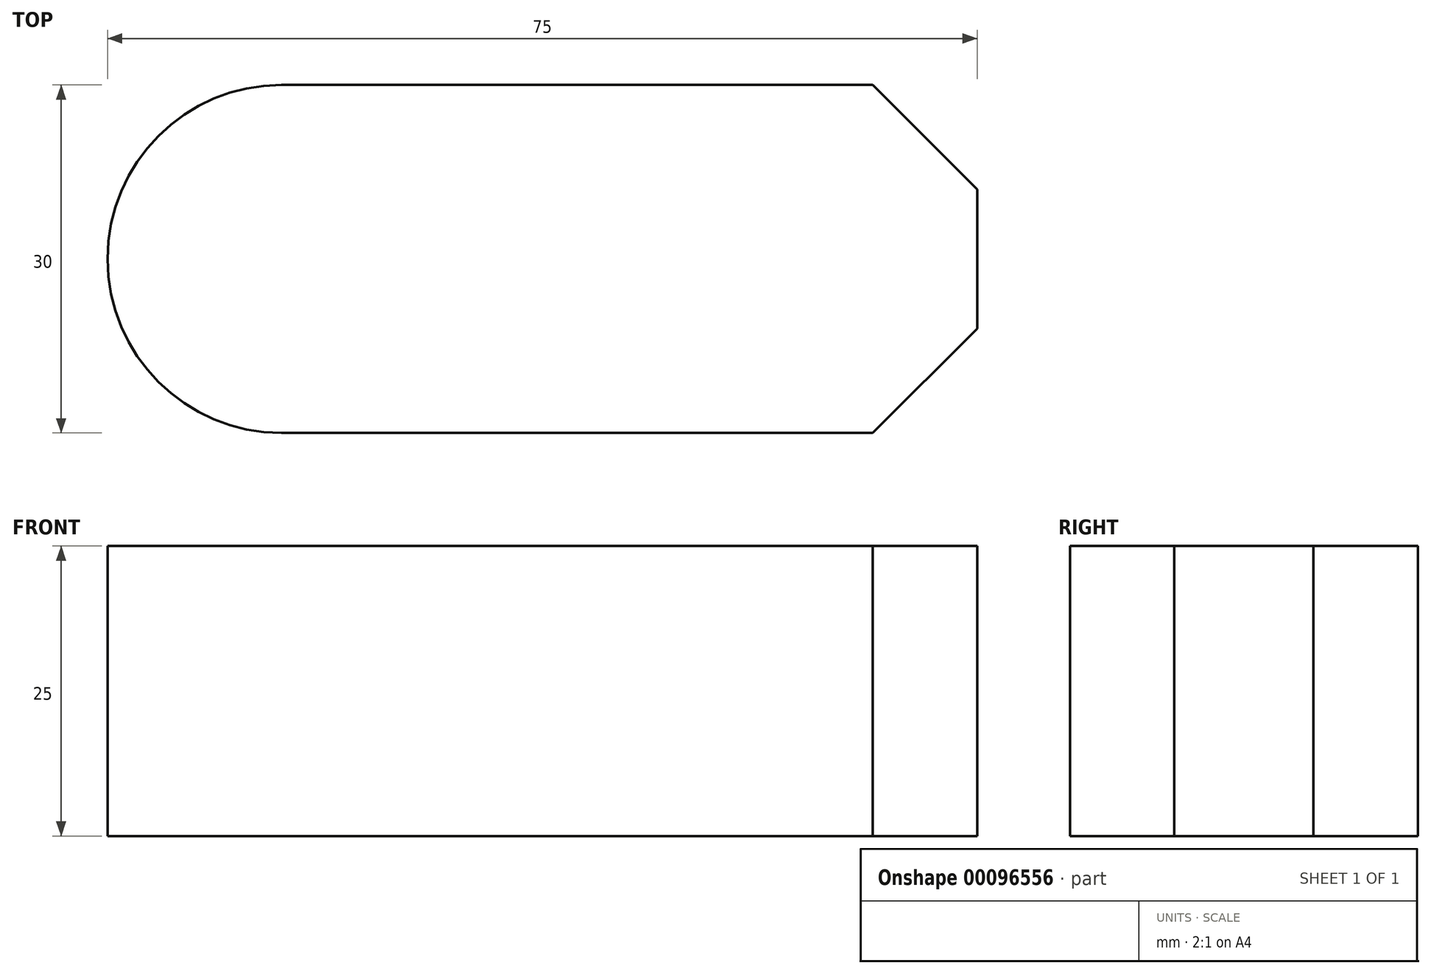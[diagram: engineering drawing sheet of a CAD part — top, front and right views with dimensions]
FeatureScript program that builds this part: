
annotation { "Feature Type Name" : "Feature", "Feature Type Description" : "" }
export const myFeature = defineFeature(function(context is Context, id is Id, definition is map)
    precondition{}
    {
        {
            var Q0;
            Q0=qCreatedBy(makeId("Top.planeOp"),FACE);
            var sketch = newSketch(context, id + "F0", { "sketchPlane" : qUnion([Q0])});
            skLineSegment(sketch, "E0.bottom", {"start": v(0, 0) * mm, "end": v(51, 0) * mm});
            skLineSegment(sketch, "E0.top", {"start": v(0, 30) * mm, "end": v(51, 30) * mm});
            skLineSegment(sketch, "E0.right", {"start": v(60, 9) * mm, "end": v(60, 21) * mm});
            skArc(sketch, "E1", {"start": v(0, 30) * mm, "mid": v(-15, 15) * mm, "end": v(0, 0) * mm});
            skLineSegment(sketch, "E2", {"start": v(51, 30) * mm, "end": v(60, 21) * mm});
            skLineSegment(sketch, "E3", {"start": v(60, 21) * mm, "end": v(60, 9) * mm});
            skLineSegment(sketch, "E4", {"start": v(60, 9) * mm, "end": v(51, 0) * mm});
            skSolve(sketch);
        }
        {
            var Q0;
            Q0=makeQuery(id+"F0.imprint","IMPRINT",FACE,{"disambiguationData":[TD([[makeQuery(id+"F0.imprint","IMPRINT",EDGE,{"derivedFrom":sQuery(id+"F0.wireOp",EDGE,"E0.bottom")}),1.0]])]});
            extrude(context, id + "F1", {"entities" : qUnion([Q0]), "depth" : 25 * mm});
        }
    });
